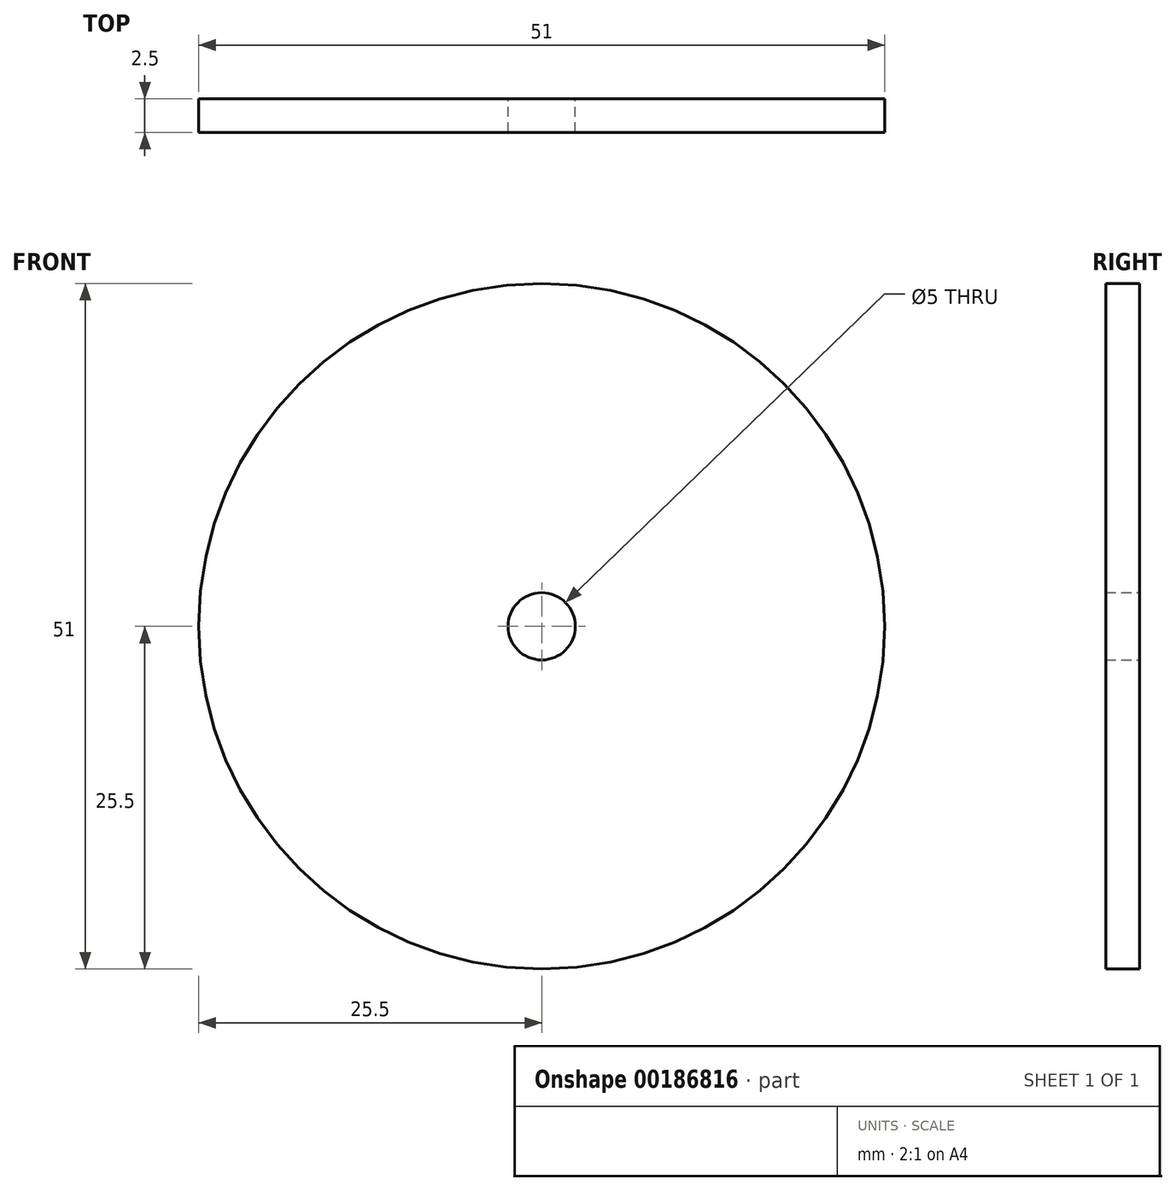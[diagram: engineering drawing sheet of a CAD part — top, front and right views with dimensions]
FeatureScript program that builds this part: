
annotation { "Feature Type Name" : "Feature", "Feature Type Description" : "" }
export const myFeature = defineFeature(function(context is Context, id is Id, definition is map)
    precondition{}
    {
        {
            var Q0;
            Q0=qCreatedBy(makeId("Front.planeOp"),FACE);
            var sketch = newSketch(context, id + "F0", { "sketchPlane" : qUnion([Q0])});
            skCircle(sketch, "E0", {"center": v(0, 0) * mm, "radius": 25.5 * mm});
            skCircle(sketch, "E1", {"center": v(0, 0) * mm, "radius": 2.5 * mm});
            skSolve(sketch);
        }
        {
            var Q0;
            Q0=makeQuery(id+"F0.imprint","IMPRINT",FACE,{"disambiguationData":[TD([[makeQuery(id+"F0.imprint","IMPRINT",EDGE,{"derivedFrom":sQuery(id+"F0.wireOp",EDGE,"E0")}),1.0]])]});
            extrude(context, id + "F1", {"entities" : qUnion([Q0]), "depth" : 2.5 * mm});
        }
    });
